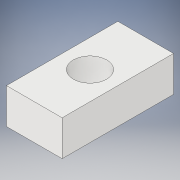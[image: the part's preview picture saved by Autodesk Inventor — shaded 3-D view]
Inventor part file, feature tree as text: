
AUTODESK INVENTOR PART (.ipt)
format: ipt  version: 2019 (Build 230136000, 136)  size: 105,472 bytes
history: native  units: mm
features: extrude x1, sketch x1
ambient origin geometry x8: Origin, YZ Plane, XZ Plane, XY Plane, X Axis, Y Axis, Z Axis, Center Point
bodies: Solid1 (feature_tree)
feature tree (2):
  extrude  "Extrusion1"  Depth=10.0mm
  sketch  "Sketch1"  dims[d0=6.0mm d1=10.0mm d2=20.0mm d3=6.36mm d4=0.0mm]
